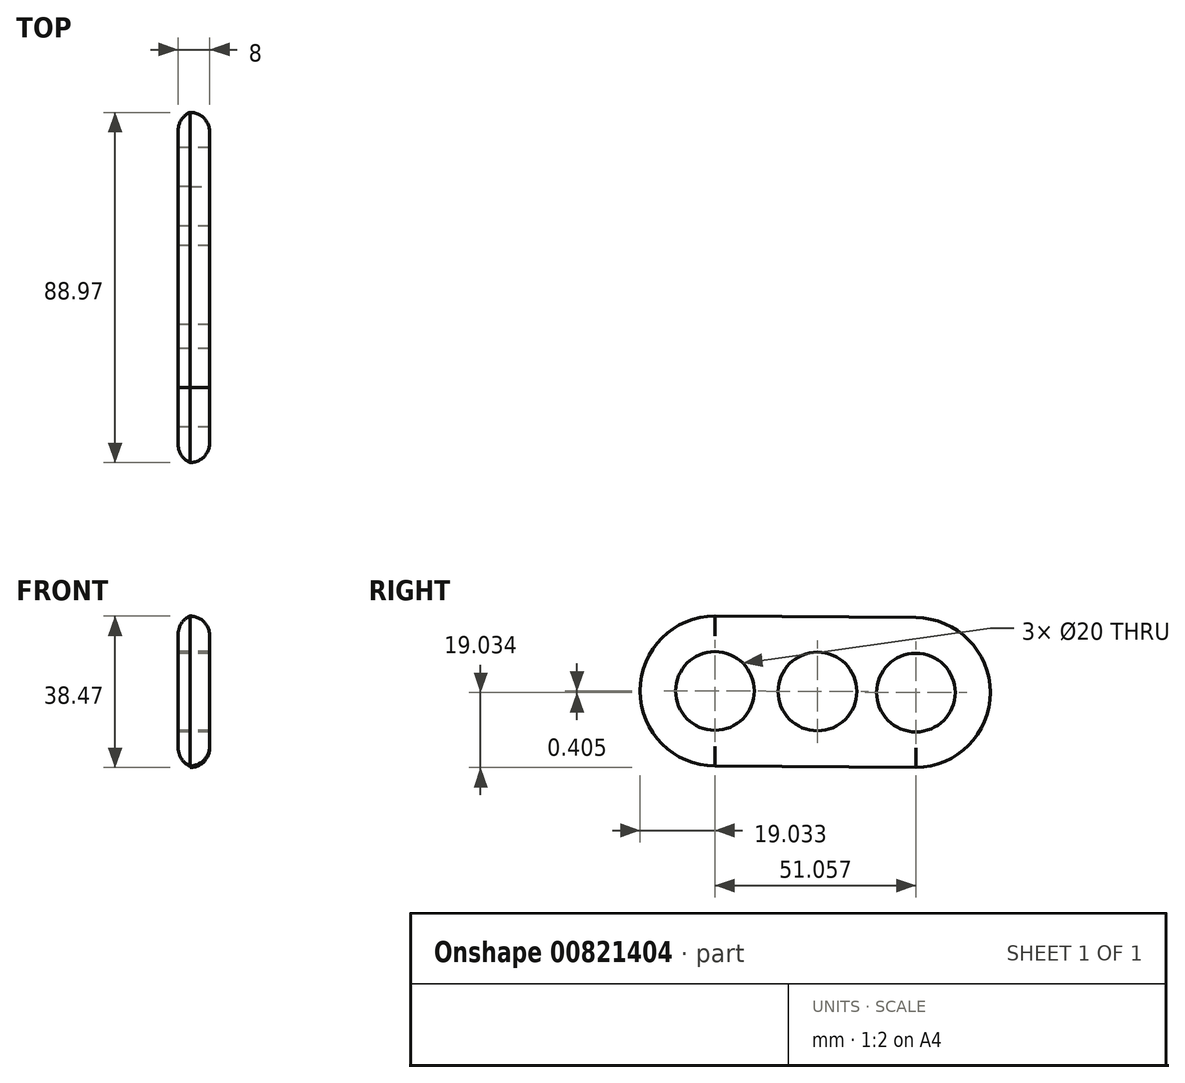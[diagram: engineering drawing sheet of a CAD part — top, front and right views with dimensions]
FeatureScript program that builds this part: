
annotation { "Feature Type Name" : "Feature", "Feature Type Description" : "" }
export const myFeature = defineFeature(function(context is Context, id is Id, definition is map)
    precondition{}
    {
        {
            var Q0;
            Q0=qCreatedBy(makeId("Right.planeOp"),FACE);
            var sketch = newSketch(context, id + "F0", { "sketchPlane" : qUnion([Q0])});
            skCircle(sketch, "E0", {"center": v(0, 0) * mm, "radius": 10 * mm});
            skCircle(sketch, "E1", {"center": v(-26.06, 0.14) * mm, "radius": 10 * mm});
            skCircle(sketch, "E2", {"center": v(25, -0.27) * mm, "radius": 10 * mm});
            skArc(sketch, "E3", {"start": v(-26.06, 19.17) * mm, "mid": v(-45.09, 0.14) * mm, "end": v(-26.06, -18.9) * mm});
            skLineSegment(sketch, "E4", {"start": v(-26.06, 19.17) * mm, "end": v(25, 18.76) * mm});
            skLineSegment(sketch, "E5", {"start": v(-26.06, -18.9) * mm, "end": v(25, -19.3) * mm});
            skArc(sketch, "E6", {"start": v(25, -19.3) * mm, "mid": v(43.88, -0.27) * mm, "end": v(25, 18.76) * mm});
            skSolve(sketch);
        }
        {
            var Q0;
            Q0 = qSketchRegion(id + "F0", true);
            extrude(context, id + "F1", {"entities" : qUnion([Q0]), "depth" : 8 * mm, "offsetDistance" : 25 * mm});
        }
        {
            var Q0;
            Q0=makeQuery(id+"F1.opExtrude","CAP_EDGE",EDGE,{"disambiguationData":[OSD([sQuery(id+"F0.wireOp",EDGE,"E4")])],"isStart":false});
            var Q1;
            Q1=makeQuery(id+"F1.opExtrude","CAP_EDGE",EDGE,{"disambiguationData":[OSD([sQuery(id+"F0.wireOp",EDGE,"E6")])],"isStart":false});
            var Q2;
            Q2=makeQuery(id+"F1.opExtrude","CAP_EDGE",EDGE,{"disambiguationData":[OSD([sQuery(id+"F0.wireOp",EDGE,"E3")])],"isStart":false});
            fillet(context, id + "F2", {"entities" : qUnion([Q0, Q1, Q2]), "radius" : 5 * mm, "tangentPropagation" : true, "allowEdgeOverflow" : false});
        }
        {
            var Q0;
            Q0=makeQuery(id+"F1.opExtrude","CAP_EDGE",EDGE,{"disambiguationData":[OSD([sQuery(id+"F0.wireOp",EDGE,"E4")])],"isStart":true});
            var Q1;
            Q1=makeQuery(id+"F1.opExtrude","CAP_EDGE",EDGE,{"disambiguationData":[OSD([sQuery(id+"F0.wireOp",EDGE,"E5")])],"isStart":true});
            var Q2;
            Q2=makeQuery(id+"F1.opExtrude","CAP_EDGE",EDGE,{"disambiguationData":[OSD([sQuery(id+"F0.wireOp",EDGE,"E3")])],"isStart":true});
            fillet(context, id + "F3", {"entities" : qUnion([Q0, Q1, Q2]), "radius" : 5 * mm, "tangentPropagation" : true, "allowEdgeOverflow" : false});
        }
    });
